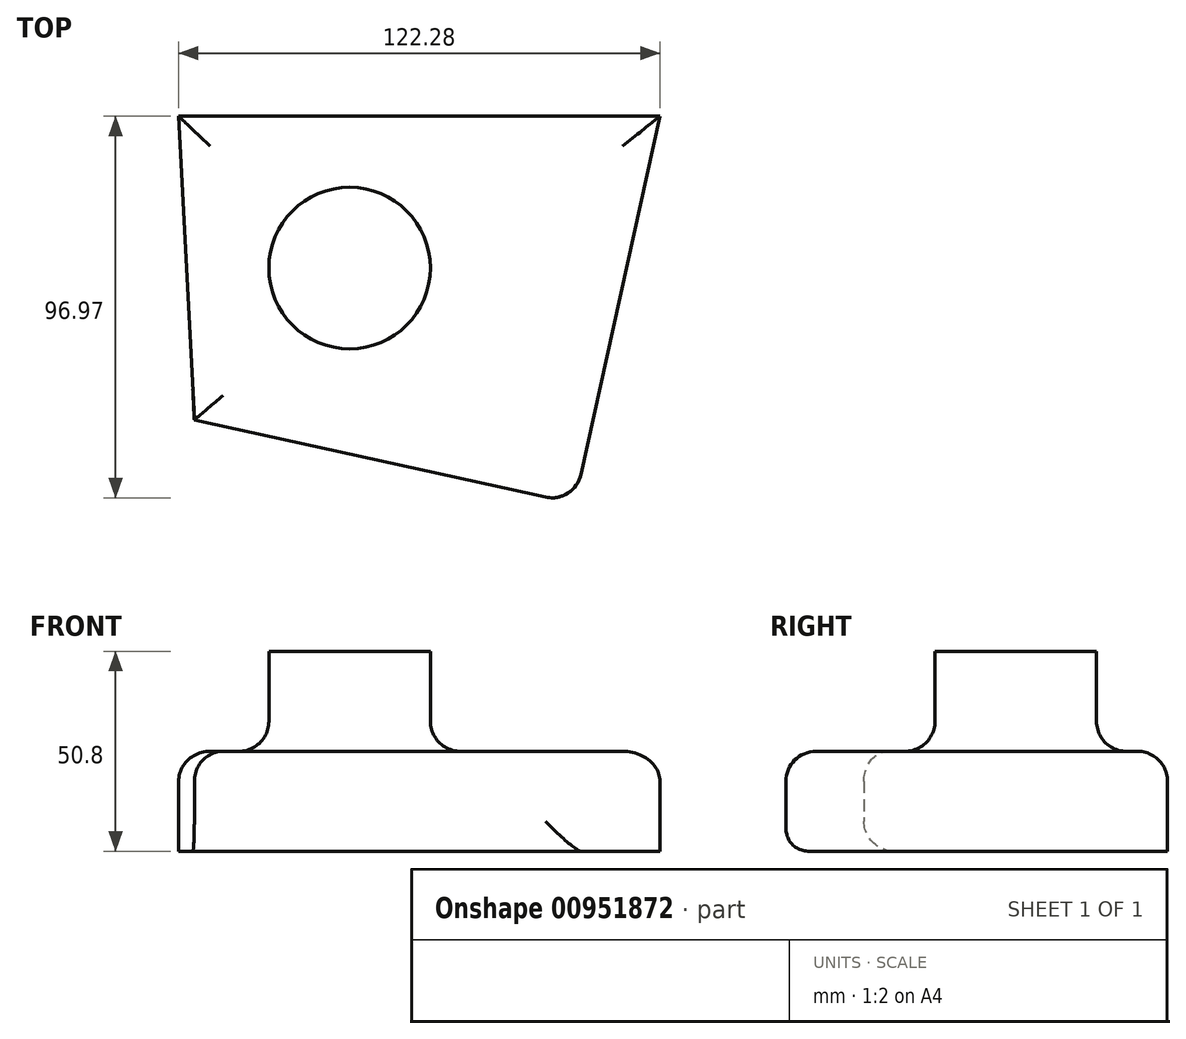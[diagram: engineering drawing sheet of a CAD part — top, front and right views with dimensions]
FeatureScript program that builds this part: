
annotation { "Feature Type Name" : "Feature", "Feature Type Description" : "" }
export const myFeature = defineFeature(function(context is Context, id is Id, definition is map)
    precondition{}
    {
        {
            var Q0;
            Q0=qCreatedBy(makeId("Top.planeOp"),FACE);
            var sketch = newSketch(context, id + "F0", { "sketchPlane" : qUnion([Q0])});
            skLineSegment(sketch, "E0", {"start": v(-57.25, 60.46) * mm, "end": v(65.03, 60.46) * mm});
            skLineSegment(sketch, "E1", {"start": v(65.03, 60.46) * mm, "end": v(43.34, -37.97) * mm});
            skLineSegment(sketch, "E2", {"start": v(43.34, -37.97) * mm, "end": v(-53.26, -16.69) * mm});
            skLineSegment(sketch, "E3", {"start": v(-53.26, -16.69) * mm, "end": v(-57.25, 60.46) * mm});
            skSolve(sketch);
        }
        {
            var Q0;
            Q0 = qSketchRegion(id + "F0", true);
            extrude(context, id + "F1", {"entities" : qUnion([Q0]), "depth" : 25.4 * mm, "offsetDistance" : 25.4 * mm});
        }
        {
            var Q0;
            Q0=makeQuery(id+"F1.opExtrude","CAP_FACE",FACE,{"disambiguationData":[OSD([sQuery(id+"F0.wireOp",EDGE,"E0"),sQuery(id+"F0.wireOp",EDGE,"E1"),sQuery(id+"F0.wireOp",EDGE,"E2"),sQuery(id+"F0.wireOp",EDGE,"E3")])],"isStart":false});
            var sketch = newSketch(context, id + "F2", { "sketchPlane" : qUnion([Q0])});
            skCircle(sketch, "E4", {"center": v(-13.8, 21.89) * mm, "radius": 20.52 * mm});
            skPoint(sketch, "E4.centerSnap0", {"position": v(-55.25, 21.89) * mm});
            skSolve(sketch);
        }
        {
            var Q0;
            Q0 = qSketchRegion(id + "F2", true);
            extrude(context, id + "F3", {"entities" : qUnion([Q0]), "operationType" : NewBodyOperationType.ADD, "depth" : 25.4 * mm, "offsetDistance" : 25.4 * mm});
        }
        {
            var Q0;
            Q0=makeQuery(id+"F1.opExtrude","CAP_EDGE",EDGE,{"disambiguationData":[OSD([sQuery(id+"F0.wireOp",EDGE,"E1")])],"isStart":false});
            var Q1;
            Q1=makeQuery(id+"F1.opExtrude","CAP_FACE",FACE,{"disambiguationData":[OSD([sQuery(id+"F0.wireOp",EDGE,"E0"),sQuery(id+"F0.wireOp",EDGE,"E1"),sQuery(id+"F0.wireOp",EDGE,"E2"),sQuery(id+"F0.wireOp",EDGE,"E3")])],"isStart":false});
            var Q2;
            Q2=makeQuery(id+"F1.opExtrude","CAP_EDGE",EDGE,{"disambiguationData":[OSD([sQuery(id+"F0.wireOp",EDGE,"E2")])],"isStart":false});
            var Q3;
            Q3=makeQuery(id+"F1.opExtrude","SWEPT_EDGE",EDGE,{"disambiguationData":[OSD([sQuery(id+"F0.wireOp",EDGE,"E1"),sQuery(id+"F0.wireOp",EDGE,"E2")])]});
            var Q4;
            Q4=makeQuery(id+"F1.opExtrude","CAP_EDGE",EDGE,{"disambiguationData":[OSD([sQuery(id+"F0.wireOp",EDGE,"E2")])],"isStart":true});
            fillet(context, id + "F4", {"entities" : qUnion([Q0, Q1, Q2, Q3, Q4]), "radius" : 7.62 * mm, "tangentPropagation" : true, "allowEdgeOverflow" : false});
        }
        {
            var Q0;
            Q0=makeQuery(id+"F3.opExtrude","CAP_FACE",FACE,{"disambiguationData":[OSD([sQuery(id+"F2.wireOp",EDGE,"E4")])],"isStart":false});
            var Q1;
            Q1=makeQuery(id+"F1.opExtrude","SWEPT_FACE",FACE,{"disambiguationData":[OSD([sQuery(id+"F0.wireOp",EDGE,"E0")])]});
            var Q2;
            Q2=makeQuery(id+"F1.opExtrude","SWEPT_EDGE",EDGE,{"disambiguationData":[OSD([sQuery(id+"F0.wireOp",EDGE,"E0"),sQuery(id+"F0.wireOp",EDGE,"E1")])]});
            var Q3;
            Q3=makeQuery(id+"F1.opExtrude","CAP_EDGE",EDGE,{"disambiguationData":[OSD([sQuery(id+"F0.wireOp",EDGE,"E0")])],"isStart":true});
            revolve(context, id + "F5", {"bodyType" : ToolBodyType.SURFACE, "surfaceOperationType" : NewSurfaceOperationType.NEW, "entities" : qUnion([Q0, Q1]), "surfaceEntities" : qUnion([Q2]), "axis" : qUnion([Q3]), "revolveType" : RevolveType.FULL});
        }
    });
